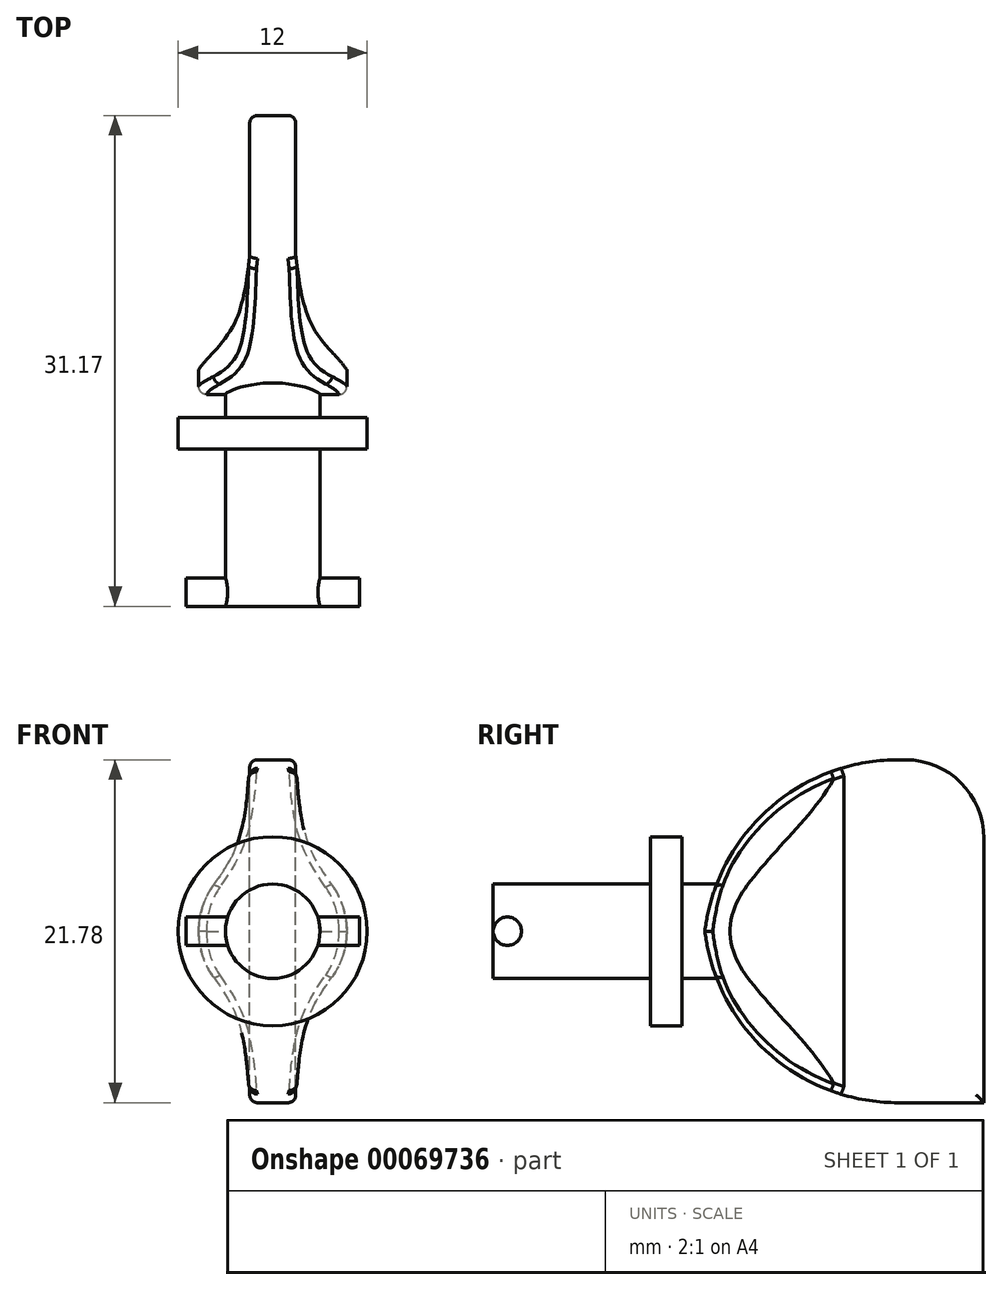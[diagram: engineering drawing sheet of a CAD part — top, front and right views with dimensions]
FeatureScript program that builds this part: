
annotation { "Feature Type Name" : "Feature", "Feature Type Description" : "" }
export const myFeature = defineFeature(function(context is Context, id is Id, definition is map)
    precondition{}
    {
        {
            var Q0;
            Q0=qCreatedBy(makeId("Front.planeOp"),FACE);
            var sketch = newSketch(context, id + "F0", { "sketchPlane" : qUnion([Q0])});
            skCircle(sketch, "E0", {"center": v(0, 0) * mm, "radius": 3 * mm});
            skSolve(sketch);
        }
        {
            var Q0;
            Q0 = qSketchRegion(id + "F0", true);
            extrude(context, id + "F1", {"entities" : qUnion([Q0]), "depth" : 10 * mm});
        }
        {
            var Q0;
            Q0=qCreatedBy(makeId("Right.planeOp"),FACE);
            var sketch = newSketch(context, id + "F2", { "sketchPlane" : qUnion([Q0])});
            skCircle(sketch, "E1", {"center": v(-9.1, 0) * mm, "radius": 0.9 * mm});
            skSolve(sketch);
        }
        {
            var Q0;
            Q0 = qSketchRegion(id + "F2", true);
            extrude(context, id + "F3", {"entities" : qUnion([Q0]), "operationType" : NewBodyOperationType.ADD, "endBound" : BoundingType.SYMMETRIC, "depth" : 11 * mm});
        }
        {
            var Q0;
            Q0=qCreatedBy(makeId("Front.planeOp"),FACE);
            var sketch = newSketch(context, id + "F4", { "sketchPlane" : qUnion([Q0])});
            skCircle(sketch, "E2", {"center": v(0, 0) * mm, "radius": 6 * mm});
            skSolve(sketch);
        }
        {
            var Q0;
            Q0 = qSketchRegion(id + "F4", true);
            extrude(context, id + "F5", {"entities" : qUnion([Q0]), "operationType" : NewBodyOperationType.ADD, "oppositeDirection" : true, "depth" : 2 * mm});
        }
        {
            var Q0;
            Q0=qCreatedBy(makeId("Front.planeOp"),FACE);
            var sketch = newSketch(context, id + "F6", { "sketchPlane" : qUnion([Q0])});
            skCircle(sketch, "E3", {"center": v(0, 0) * mm, "radius": 3 * mm});
            skSolve(sketch);
        }
        {
            var Q0;
            Q0 = qSketchRegion(id + "F6", true);
            extrude(context, id + "F7", {"entities" : qUnion([Q0]), "operationType" : NewBodyOperationType.ADD, "oppositeDirection" : true, "depth" : 4 * mm});
        }
        {
            var Q0;
            Q0=qCreatedBy(makeId("Right.planeOp"),FACE);
            var sketch = newSketch(context, id + "F8", { "sketchPlane" : qUnion([Q0])});
            skLineSegment(sketch, "E4.bottom", {"start": v(3.36, 10.9) * mm, "end": v(21.17, 10.9) * mm});
            skLineSegment(sketch, "E4.top", {"start": v(3.36, -12.24) * mm, "end": v(21.17, -12.24) * mm});
            skLineSegment(sketch, "E4.left", {"start": v(3.36, 10.9) * mm, "end": v(3.36, -12.24) * mm});
            skLineSegment(sketch, "E4.right", {"start": v(21.17, 10.9) * mm, "end": v(21.17, -12.24) * mm});
            skSolve(sketch);
        }
        {
            var Q0;
            Q0 = qSketchRegion(id + "F8", true);
            extrude(context, id + "F9", {"entities" : qUnion([Q0]), "operationType" : NewBodyOperationType.ADD, "endBound" : BoundingType.SYMMETRIC, "depth" : 13 * mm});
        }
        {
            var Q0;
            Q0=makeQuery(id+"F9.opExtrude","SWEPT_FACE",FACE,{"disambiguationData":[OSD([sQuery(id+"F8.wireOp",EDGE,"E4.right")])]});
            var sketch = newSketch(context, id + "F10", { "sketchPlane" : qUnion([Q0])});
            skFitSpline(sketch, "E5", {"points": [v(5.08, 0) * mm, v(4.54, 1.74) * mm, v(2.44, 5.09) * mm, v(1.46, 10.9) * mm], "startDerivative": vector(-1.3, 7.15) * mm, "endDerivative": vector(-0.86, 14.8) * mm});
            skLineSegment(sketch, "E6", {"start": v(1.46, 10.9) * mm, "end": v(6.5, 10.9) * mm});
            skLineSegment(sketch, "E7", {"start": v(6.5, 10.9) * mm, "end": v(6.5, 0) * mm});
            skLineSegment(sketch, "E8", {"start": v(6.5, 0) * mm, "end": v(5.08, 0) * mm});
            skFitSpline(sketch, "E9.MirrorCS", {"points": [v(-5.08, 0) * mm, v(-4.54, 1.74) * mm, v(-2.44, 5.09) * mm, v(-1.46, 10.9) * mm], "startDerivative": vector(1.3, 7.15) * mm, "endDerivative": vector(0.86, 14.8) * mm});
            skLineSegment(sketch, "E10.MirrorCS", {"start": v(-1.46, 10.9) * mm, "end": v(-6.5, 10.9) * mm});
            skLineSegment(sketch, "E11.MirrorCS", {"start": v(-6.5, 10.9) * mm, "end": v(-6.5, 0) * mm});
            skLineSegment(sketch, "E12.MirrorCS", {"start": v(-6.5, 0) * mm, "end": v(-5.08, 0) * mm});
            skFitSpline(sketch, "E13.MirrorCS", {"points": [v(-5.08, 0) * mm, v(-4.54, -1.74) * mm, v(-2.44, -5.09) * mm, v(-1.46, -10.9) * mm], "startDerivative": vector(1.3, -7.15) * mm, "endDerivative": vector(0.86, -14.8) * mm});
            skFitSpline(sketch, "E14.MirrorCS", {"points": [v(5.08, 0) * mm, v(4.54, -1.74) * mm, v(2.44, -5.09) * mm, v(1.46, -10.9) * mm], "startDerivative": vector(-1.3, -7.15) * mm, "endDerivative": vector(-0.86, -14.8) * mm});
            skLineSegment(sketch, "E15.MirrorCS", {"start": v(6.5, -10.9) * mm, "end": v(6.5, 0) * mm});
            skLineSegment(sketch, "E16.MirrorCS", {"start": v(-1.46, -10.9) * mm, "end": v(-6.5, -10.9) * mm});
            skLineSegment(sketch, "E17.MirrorCS", {"start": v(1.46, -10.9) * mm, "end": v(6.5, -10.9) * mm});
            skSolve(sketch);
        }
        {
            var Q0;
            Q0=makeQuery(id+"F10.imprint","IMPRINT",FACE,{"disambiguationData":[TD([[makeQuery(id+"F10.imprint","IMPRINT",EDGE,{"derivedFrom":sQuery(id+"F10.wireOp",EDGE,"E5")}),-1.0]])]});
            var Q1;
            Q1=makeQuery(id+"F10.imprint","IMPRINT",FACE,{"disambiguationData":[TD([[makeQuery(id+"F10.imprint","IMPRINT",EDGE,{"derivedFrom":sQuery(id+"F10.wireOp",EDGE,"E9.MirrorCS")}),1.0]])]});
            var Q2;
            {var subQ0=sQuery(id+"F10.wireOp",EDGE,"E12.MirrorCS");Q2=makeQuery(id+"F10.imprint","IMPRINT",FACE,{"disambiguationData":[TD([[makeQuery(id+"F10.imprint","IMPRINT",EDGE,{"derivedFrom":subQ0}),-1.0]])]});}
            var Q3;
            Q3=makeQuery(id+"F10.imprint","IMPRINT",FACE,{"disambiguationData":[TD([[makeQuery(id+"F10.imprint","IMPRINT",EDGE,{"derivedFrom":sQuery(id+"F10.wireOp",EDGE,"E8")}),1.0]])]});
            extrude(context, id + "F11", {"entities" : qUnion([Q0, Q1, Q2, Q3]), "operationType" : NewBodyOperationType.REMOVE, "oppositeDirection" : true, "depth" : 18.1 * mm});
        }
        {
            var Q0;
            Q0=makeQuery(id+"F9.opExtrude","SWEPT_FACE",FACE,{"disambiguationData":[OSD([sQuery(id+"F8.wireOp",EDGE,"E4.right")])]});
            var sketch = newSketch(context, id + "F12", { "sketchPlane" : qUnion([Q0])});
            skLineSegment(sketch, "E18.bottom", {"start": v(-6.5, -10.9) * mm, "end": v(6.5, -10.9) * mm});
            skLineSegment(sketch, "E18.top", {"start": v(-6.5, -12.24) * mm, "end": v(6.5, -12.24) * mm});
            skLineSegment(sketch, "E18.left", {"start": v(-6.5, -10.9) * mm, "end": v(-6.5, -12.24) * mm});
            skLineSegment(sketch, "E18.right", {"start": v(6.5, -10.9) * mm, "end": v(6.5, -12.24) * mm});
            skSolve(sketch);
        }
        {
            var Q0;
            Q0 = qSketchRegion(id + "F12", true);
            extrude(context, id + "F13", {"entities" : qUnion([Q0]), "operationType" : NewBodyOperationType.REMOVE, "oppositeDirection" : true, "depth" : 25 * mm});
        }
        {
            var Q0;
            Q0=makeQuery(id+"F9.opExtrude","SWEPT_FACE",FACE,{"disambiguationData":[OSD([sQuery(id+"F8.wireOp",EDGE,"E4.bottom")])]});
            var sketch = newSketch(context, id + "F14", { "sketchPlane" : qUnion([Q0])});
            skFitSpline(sketch, "E19", {"points": [v(-5.1, 3.39) * mm, v(-4.84, 4.81) * mm, v(-2.65, 7.57) * mm, v(-1.46, 12.27) * mm], "startDerivative": vector(-0.1, 6.11) * mm, "endDerivative": vector(1.43, 12.16) * mm});
            skLineSegment(sketch, "E20", {"start": v(-1.46, 12.27) * mm, "end": v(-1.46, 21.17) * mm});
            skLineSegment(sketch, "E21", {"start": v(-1.46, 21.17) * mm, "end": v(-5.2, 21.17) * mm});
            skLineSegment(sketch, "E22", {"start": v(-5.2, 21.17) * mm, "end": v(-5.1, 3.39) * mm});
            skLineSegment(sketch, "E23.MirrorCS", {"start": v(5.2, 21.17) * mm, "end": v(5.1, 3.39) * mm});
            skLineSegment(sketch, "E24.MirrorCS", {"start": v(1.46, 12.27) * mm, "end": v(1.46, 21.17) * mm});
            skLineSegment(sketch, "E25.MirrorCS", {"start": v(1.46, 21.17) * mm, "end": v(5.2, 21.17) * mm});
            skFitSpline(sketch, "E26.MirrorCS", {"points": [v(5.1, 3.39) * mm, v(4.84, 4.81) * mm, v(2.65, 7.57) * mm, v(1.46, 12.27) * mm], "startDerivative": vector(0.1, 6.11) * mm, "endDerivative": vector(-1.43, 12.16) * mm});
            skSolve(sketch);
        }
        {
            var Q0;
            Q0 = qSketchRegion(id + "F14", true);
            extrude(context, id + "F15", {"entities" : qUnion([Q0]), "operationType" : NewBodyOperationType.REMOVE, "oppositeDirection" : true, "depth" : 25 * mm});
        }
        {
            var Q0;
            Q0=makeQuery(id+"F9.opExtrude","SWEPT_EDGE",EDGE,{"disambiguationData":[OSD([sQuery(id+"F8.wireOp",EDGE,"E4.bottom"),sQuery(id+"F8.wireOp",EDGE,"E4.right")])]});
            var Q1;
            Q1=makeQuery(id+"F13.boolean.opBoolean","COPY",EDGE,{"derivedFrom":makeQuery(id+"F13.opExtrude","CAP_EDGE",EDGE,{"disambiguationData":[OSD([sQuery(id+"F12.wireOp",EDGE,"E18.bottom")])],"isStart":true})});
            fillet(context, id + "F16", {"entities" : qUnion([Q0, Q1]), "radius" : 5 * mm, "tangentPropagation" : true, "allowEdgeOverflow" : false});
        }
        {
            var Q0;
            Q0=makeQuery(id+"F9.opExtrude","SWEPT_EDGE",EDGE,{"disambiguationData":[OSD([sQuery(id+"F8.wireOp",EDGE,"E4.bottom"),sQuery(id+"F8.wireOp",EDGE,"E4.left")])]});
            var Q1;
            Q1=makeQuery(id+"F13.boolean.opBoolean","INTERSECT",EDGE,{"derivedFrom":[makeQuery(id+"F9.opExtrude","SWEPT_FACE",FACE,{"disambiguationData":[OSD([sQuery(id+"F8.wireOp",EDGE,"E4.left")])]}),makeQuery(id+"F13.opExtrude","SWEPT_FACE",FACE,{"disambiguationData":[OSD([sQuery(id+"F12.wireOp",EDGE,"E18.bottom")])]})]});
            fillet(context, id + "F17", {"entities" : qUnion([Q0, Q1]), "radius" : 12.37 * mm, "tangentPropagation" : true, "allowEdgeOverflow" : false});
        }
        {
            var Q0;
            Q0=makeQuery(id+"F11.boolean.opBoolean","COPY",EDGE,{"derivedFrom":makeQuery(id+"F11.opExtrude","SWEPT_EDGE",EDGE,{"disambiguationData":[OSD([sQuery(id+"F10.wireOp",EDGE,"E9.MirrorCS"),sQuery(id+"F10.wireOp",EDGE,"E12.MirrorCS"),sQuery(id+"F10.wireOp",EDGE,"E13.MirrorCS")])]})});
            fillet(context, id + "F18", {"entities" : qUnion([Q0]), "radius" : 5 * mm, "tangentPropagation" : true, "allowEdgeOverflow" : false});
        }
        {
            var Q0;
            Q0=makeQuery(id+"F11.boolean.opBoolean","COPY",EDGE,{"derivedFrom":makeQuery(id+"F11.opExtrude","SWEPT_EDGE",EDGE,{"disambiguationData":[OSD([sQuery(id+"F10.wireOp",EDGE,"E5"),sQuery(id+"F10.wireOp",EDGE,"E8"),sQuery(id+"F10.wireOp",EDGE,"E14.MirrorCS")])]})});
            fillet(context, id + "F19", {"entities" : qUnion([Q0]), "radius" : 5 * mm, "tangentPropagation" : true, "allowEdgeOverflow" : false});
        }
        {
            var Q0;
            Q0=makeQuery(id+"F19.opFillet","BLEND_EDGE",EDGE,{"blendedFrom":[makeQuery(id+"F11.boolean.opBoolean","COPY",EDGE,{"derivedFrom":makeQuery(id+"F11.opExtrude","SWEPT_EDGE",EDGE,{"disambiguationData":[OSD([sQuery(id+"F10.wireOp",EDGE,"E5"),sQuery(id+"F10.wireOp",EDGE,"E8"),sQuery(id+"F10.wireOp",EDGE,"E14.MirrorCS")])]})}),makeQuery(id+"F17.opFillet","BLEND_FACE",FACE,{"disambiguationData":[OSD([sQuery(id+"F8.wireOp",EDGE,"E4.bottom"),sQuery(id+"F8.wireOp",EDGE,"E4.left")])]})],"blendedInto":[makeQuery(id+"F17.opFillet","BLEND_FACE",FACE,{"disambiguationData":[OSD([sQuery(id+"F8.wireOp",EDGE,"E4.bottom"),sQuery(id+"F8.wireOp",EDGE,"E4.left")])]})]});
            var Q1;
            Q1=makeQuery(id+"F19.opFillet","BLEND_EDGE",EDGE,{"blendedFrom":[makeQuery(id+"F11.boolean.opBoolean","COPY",EDGE,{"derivedFrom":makeQuery(id+"F11.opExtrude","SWEPT_EDGE",EDGE,{"disambiguationData":[OSD([sQuery(id+"F10.wireOp",EDGE,"E5"),sQuery(id+"F10.wireOp",EDGE,"E8"),sQuery(id+"F10.wireOp",EDGE,"E14.MirrorCS")])]})}),makeQuery(id+"F17.opFillet","BLEND_FACE",FACE,{"disambiguationData":[OSD([sQuery(id+"F8.wireOp",EDGE,"E4.left"),sQuery(id+"F12.wireOp",EDGE,"E18.bottom")])]})],"blendedInto":[makeQuery(id+"F17.opFillet","BLEND_FACE",FACE,{"disambiguationData":[OSD([sQuery(id+"F8.wireOp",EDGE,"E4.left"),sQuery(id+"F12.wireOp",EDGE,"E18.bottom")])]})]});
            var Q2;
            Q2=makeQuery(id+"F17.opFillet","BLEND_EDGE",EDGE,{"blendedFrom":[makeQuery(id+"F13.boolean.opBoolean","INTERSECT",EDGE,{"derivedFrom":[makeQuery(id+"F9.opExtrude","SWEPT_FACE",FACE,{"disambiguationData":[OSD([sQuery(id+"F8.wireOp",EDGE,"E4.left")])]}),makeQuery(id+"F13.opExtrude","SWEPT_FACE",FACE,{"disambiguationData":[OSD([sQuery(id+"F12.wireOp",EDGE,"E18.bottom")])]})]}),makeQuery(id+"F11.boolean.opBoolean","COPY",FACE,{"derivedFrom":makeQuery(id+"F11.opExtrude","SWEPT_FACE",FACE,{"disambiguationData":[OSD([sQuery(id+"F10.wireOp",EDGE,"E14.MirrorCS")])]})})],"blendedInto":[makeQuery(id+"F11.boolean.opBoolean","COPY",FACE,{"derivedFrom":makeQuery(id+"F11.opExtrude","SWEPT_FACE",FACE,{"disambiguationData":[OSD([sQuery(id+"F10.wireOp",EDGE,"E14.MirrorCS")])]})})]});
            var Q3;
            Q3=makeQuery(id+"F17.opFillet","BLEND_EDGE",EDGE,{"blendedFrom":[makeQuery(id+"F13.boolean.opBoolean","INTERSECT",EDGE,{"derivedFrom":[makeQuery(id+"F9.opExtrude","SWEPT_FACE",FACE,{"disambiguationData":[OSD([sQuery(id+"F8.wireOp",EDGE,"E4.left")])]}),makeQuery(id+"F13.opExtrude","SWEPT_FACE",FACE,{"disambiguationData":[OSD([sQuery(id+"F12.wireOp",EDGE,"E18.bottom")])]})]}),makeQuery(id+"F15.boolean.opBoolean","COPY",FACE,{"derivedFrom":makeQuery(id+"F15.opExtrude","SWEPT_FACE",FACE,{"disambiguationData":[OSD([sQuery(id+"F14.wireOp",EDGE,"E20")])]})})],"blendedInto":[makeQuery(id+"F15.boolean.opBoolean","COPY",FACE,{"derivedFrom":makeQuery(id+"F15.opExtrude","SWEPT_FACE",FACE,{"disambiguationData":[OSD([sQuery(id+"F14.wireOp",EDGE,"E20")])]})})]});
            var Q4;
            Q4=makeQuery(id+"F16.opFillet","BLEND_EDGE",EDGE,{"blendedFrom":[makeQuery(id+"F13.boolean.opBoolean","COPY",EDGE,{"derivedFrom":makeQuery(id+"F13.opExtrude","CAP_EDGE",EDGE,{"disambiguationData":[OSD([sQuery(id+"F12.wireOp",EDGE,"E18.bottom")])],"isStart":true})}),makeQuery(id+"F15.boolean.opBoolean","COPY",FACE,{"derivedFrom":makeQuery(id+"F15.opExtrude","SWEPT_FACE",FACE,{"disambiguationData":[OSD([sQuery(id+"F14.wireOp",EDGE,"E20")])]})})],"blendedInto":[makeQuery(id+"F15.boolean.opBoolean","COPY",FACE,{"derivedFrom":makeQuery(id+"F15.opExtrude","SWEPT_FACE",FACE,{"disambiguationData":[OSD([sQuery(id+"F14.wireOp",EDGE,"E20")])]})})]});
            var Q5;
            Q5=makeQuery(id+"F15.boolean.opBoolean","COPY",EDGE,{"derivedFrom":makeQuery(id+"F15.opExtrude","SWEPT_EDGE",EDGE,{"disambiguationData":[OSD([sQuery(id+"F8.wireOp",EDGE,"E4.bottom"),sQuery(id+"F8.wireOp",EDGE,"E4.right"),sQuery(id+"F14.wireOp",EDGE,"E20"),sQuery(id+"F14.wireOp",EDGE,"E21")])]})});
            var Q6;
            Q6=makeQuery(id+"F16.opFillet","BLEND_EDGE",EDGE,{"blendedFrom":[makeQuery(id+"F9.opExtrude","SWEPT_EDGE",EDGE,{"disambiguationData":[OSD([sQuery(id+"F8.wireOp",EDGE,"E4.bottom"),sQuery(id+"F8.wireOp",EDGE,"E4.right")])]}),makeQuery(id+"F15.boolean.opBoolean","COPY",FACE,{"derivedFrom":makeQuery(id+"F15.opExtrude","SWEPT_FACE",FACE,{"disambiguationData":[OSD([sQuery(id+"F14.wireOp",EDGE,"E20")])]})})],"blendedInto":[makeQuery(id+"F15.boolean.opBoolean","COPY",FACE,{"derivedFrom":makeQuery(id+"F15.opExtrude","SWEPT_FACE",FACE,{"disambiguationData":[OSD([sQuery(id+"F14.wireOp",EDGE,"E20")])]})})]});
            var Q7;
            Q7=makeQuery(id+"F17.opFillet","BLEND_EDGE",EDGE,{"blendedFrom":[makeQuery(id+"F9.opExtrude","SWEPT_EDGE",EDGE,{"disambiguationData":[OSD([sQuery(id+"F8.wireOp",EDGE,"E4.bottom"),sQuery(id+"F8.wireOp",EDGE,"E4.left")])]}),makeQuery(id+"F11.boolean.opBoolean","COPY",FACE,{"derivedFrom":makeQuery(id+"F11.opExtrude","SWEPT_FACE",FACE,{"disambiguationData":[OSD([sQuery(id+"F10.wireOp",EDGE,"E5")])]})})],"blendedInto":[makeQuery(id+"F11.boolean.opBoolean","COPY",FACE,{"derivedFrom":makeQuery(id+"F11.opExtrude","SWEPT_FACE",FACE,{"disambiguationData":[OSD([sQuery(id+"F10.wireOp",EDGE,"E5")])]})})]});
            var Q8;
            {var subQ0=sQuery(id+"F14.wireOp",EDGE,"E19");Q8=makeQuery(id+"F17.opFillet","BLEND_EDGE",EDGE,{"blendedFrom":[makeQuery(id+"F13.boolean.opBoolean","INTERSECT",EDGE,{"derivedFrom":[makeQuery(id+"F9.opExtrude","SWEPT_FACE",FACE,{"disambiguationData":[OSD([sQuery(id+"F8.wireOp",EDGE,"E4.left")])]}),makeQuery(id+"F13.opExtrude","SWEPT_FACE",FACE,{"disambiguationData":[OSD([sQuery(id+"F12.wireOp",EDGE,"E18.bottom")])]})]}),makeQuery(id+"F15.boolean.opBoolean","COPY",FACE,{"derivedFrom":makeQuery(id+"F15.opExtrude","SWEPT_FACE",FACE,{"disambiguationData":[OSD([subQ0]),TDD([makeQuery(id+"F14.imprint","IMPRINT",EDGE,{"disambiguationData":[TD([[makeQuery(id+"F14.imprint","INTERSECT",VERTEX,{"disambiguationData":[OD(1.0)],"derivedFrom":[subQ0,sQuery(id+"F14.wireOp",EDGE,"E22")]}),-1.0]])],"derivedFrom":subQ0})])]})})],"blendedInto":[makeQuery(id+"F15.boolean.opBoolean","COPY",FACE,{"derivedFrom":makeQuery(id+"F15.opExtrude","SWEPT_FACE",FACE,{"disambiguationData":[OSD([subQ0]),TDD([makeQuery(id+"F14.imprint","IMPRINT",EDGE,{"disambiguationData":[TD([[makeQuery(id+"F14.imprint","INTERSECT",VERTEX,{"disambiguationData":[OD(1.0)],"derivedFrom":[subQ0,sQuery(id+"F14.wireOp",EDGE,"E22")]}),-1.0]])],"derivedFrom":subQ0})])]})})]});}
            var Q9;
            {var subQ2=sQuery(id+"F8.wireOp",EDGE,"E4.right");var subQ3=sQuery(id+"F10.wireOp",EDGE,"E14.MirrorCS");Q9=makeQuery(id+"F15.boolean.opBoolean","SPLIT",EDGE,{"disambiguationData":[TD([makeQuery(id+"F9.opExtrude","SWEPT_FACE",FACE,{"disambiguationData":[OSD([subQ2])]})])],"derivedFrom":makeQuery(id+"F11.boolean.opBoolean","COPY",EDGE,{"derivedFrom":makeQuery(id+"F11.opExtrude","SWEPT_EDGE",EDGE,{"disambiguationData":[OSD([subQ3,sQuery(id+"F10.wireOp",EDGE,"E17.MirrorCS")])]})})});}
            var Q10;
            Q10=makeQuery(id+"F17.opFillet","BLEND_EDGE",EDGE,{"blendedFrom":[makeQuery(id+"F9.opExtrude","SWEPT_EDGE",EDGE,{"disambiguationData":[OSD([sQuery(id+"F8.wireOp",EDGE,"E4.bottom"),sQuery(id+"F8.wireOp",EDGE,"E4.left")])]}),makeQuery(id+"F15.boolean.opBoolean","COPY",FACE,{"derivedFrom":makeQuery(id+"F15.opExtrude","SWEPT_FACE",FACE,{"disambiguationData":[OSD([sQuery(id+"F14.wireOp",EDGE,"E20")])]})})],"blendedInto":[makeQuery(id+"F15.boolean.opBoolean","COPY",FACE,{"derivedFrom":makeQuery(id+"F15.opExtrude","SWEPT_FACE",FACE,{"disambiguationData":[OSD([sQuery(id+"F14.wireOp",EDGE,"E20")])]})})]});
            var Q11;
            {var subQ0=sQuery(id+"F14.wireOp",EDGE,"E19");var subQ1=sQuery(id+"F8.wireOp",EDGE,"E4.bottom");Q11=makeQuery(id+"F17.opFillet","BLEND_EDGE",EDGE,{"blendedFrom":[makeQuery(id+"F9.opExtrude","SWEPT_EDGE",EDGE,{"disambiguationData":[OSD([subQ1,sQuery(id+"F8.wireOp",EDGE,"E4.left")])]}),makeQuery(id+"F15.boolean.opBoolean","COPY",FACE,{"derivedFrom":makeQuery(id+"F15.opExtrude","SWEPT_FACE",FACE,{"disambiguationData":[OSD([subQ0]),TDD([makeQuery(id+"F14.imprint","IMPRINT",EDGE,{"disambiguationData":[TD([[makeQuery(id+"F14.imprint","INTERSECT",VERTEX,{"disambiguationData":[OD(1.0)],"derivedFrom":[subQ0,sQuery(id+"F14.wireOp",EDGE,"E22")]}),-1.0]])],"derivedFrom":subQ0})])]})})],"blendedInto":[makeQuery(id+"F15.boolean.opBoolean","COPY",FACE,{"derivedFrom":makeQuery(id+"F15.opExtrude","SWEPT_FACE",FACE,{"disambiguationData":[OSD([subQ0]),TDD([makeQuery(id+"F14.imprint","IMPRINT",EDGE,{"disambiguationData":[TD([[makeQuery(id+"F14.imprint","INTERSECT",VERTEX,{"disambiguationData":[OD(1.0)],"derivedFrom":[subQ0,sQuery(id+"F14.wireOp",EDGE,"E22")]}),-1.0]])],"derivedFrom":subQ0})])]})})]});}
            var Q12;
            Q12=makeQuery(id+"F15.boolean.opBoolean","MERGE",EDGE,{"derivedFrom":[makeQuery(id+"F11.boolean.opBoolean","COPY",EDGE,{"derivedFrom":makeQuery(id+"F11.opExtrude","SWEPT_EDGE",EDGE,{"disambiguationData":[OSD([sQuery(id+"F8.wireOp",EDGE,"E4.bottom"),sQuery(id+"F8.wireOp",EDGE,"E4.right"),sQuery(id+"F10.wireOp",EDGE,"E5"),sQuery(id+"F10.wireOp",EDGE,"E6")])]})}),makeQuery(id+"F15.opExtrude","CAP_EDGE",EDGE,{"disambiguationData":[OSD([sQuery(id+"F14.wireOp",EDGE,"E20")])],"isStart":true})]});
            fillet(context, id + "F20", {"entities" : qUnion([Q0, Q1, Q2, Q3, Q4, Q5, Q6, Q7, Q8, Q9, Q10, Q11, Q12]), "radius" : 0.5 * mm, "tangentPropagation" : true, "allowEdgeOverflow" : false});
        }
        {
            var Q0;
            Q0=makeQuery(id+"F15.boolean.opBoolean","COPY",EDGE,{"derivedFrom":makeQuery(id+"F15.opExtrude","SWEPT_EDGE",EDGE,{"disambiguationData":[OSD([sQuery(id+"F8.wireOp",EDGE,"E4.bottom"),sQuery(id+"F8.wireOp",EDGE,"E4.right"),sQuery(id+"F14.wireOp",EDGE,"E24.MirrorCS"),sQuery(id+"F14.wireOp",EDGE,"E25.MirrorCS")])]})});
            var Q1;
            Q1=makeQuery(id+"F16.opFillet","BLEND_EDGE",EDGE,{"blendedFrom":[makeQuery(id+"F9.opExtrude","SWEPT_EDGE",EDGE,{"disambiguationData":[OSD([sQuery(id+"F8.wireOp",EDGE,"E4.bottom"),sQuery(id+"F8.wireOp",EDGE,"E4.right")])]}),makeQuery(id+"F15.boolean.opBoolean","COPY",FACE,{"derivedFrom":makeQuery(id+"F15.opExtrude","SWEPT_FACE",FACE,{"disambiguationData":[OSD([sQuery(id+"F14.wireOp",EDGE,"E24.MirrorCS")])]})})],"blendedInto":[makeQuery(id+"F15.boolean.opBoolean","COPY",FACE,{"derivedFrom":makeQuery(id+"F15.opExtrude","SWEPT_FACE",FACE,{"disambiguationData":[OSD([sQuery(id+"F14.wireOp",EDGE,"E24.MirrorCS")])]})})]});
            var Q2;
            Q2=makeQuery(id+"F17.opFillet","BLEND_EDGE",EDGE,{"blendedFrom":[makeQuery(id+"F9.opExtrude","SWEPT_EDGE",EDGE,{"disambiguationData":[OSD([sQuery(id+"F8.wireOp",EDGE,"E4.bottom"),sQuery(id+"F8.wireOp",EDGE,"E4.left")])]}),makeQuery(id+"F15.boolean.opBoolean","COPY",FACE,{"derivedFrom":makeQuery(id+"F15.opExtrude","SWEPT_FACE",FACE,{"disambiguationData":[OSD([sQuery(id+"F14.wireOp",EDGE,"E24.MirrorCS")])]})})],"blendedInto":[makeQuery(id+"F15.boolean.opBoolean","COPY",FACE,{"derivedFrom":makeQuery(id+"F15.opExtrude","SWEPT_FACE",FACE,{"disambiguationData":[OSD([sQuery(id+"F14.wireOp",EDGE,"E24.MirrorCS")])]})})]});
            var Q3;
            Q3=makeQuery(id+"F17.opFillet","BLEND_EDGE",EDGE,{"blendedFrom":[makeQuery(id+"F9.opExtrude","SWEPT_EDGE",EDGE,{"disambiguationData":[OSD([sQuery(id+"F8.wireOp",EDGE,"E4.bottom"),sQuery(id+"F8.wireOp",EDGE,"E4.left")])]}),makeQuery(id+"F11.boolean.opBoolean","COPY",FACE,{"derivedFrom":makeQuery(id+"F11.opExtrude","SWEPT_FACE",FACE,{"disambiguationData":[OSD([sQuery(id+"F10.wireOp",EDGE,"E9.MirrorCS")])]})})],"blendedInto":[makeQuery(id+"F11.boolean.opBoolean","COPY",FACE,{"derivedFrom":makeQuery(id+"F11.opExtrude","SWEPT_FACE",FACE,{"disambiguationData":[OSD([sQuery(id+"F10.wireOp",EDGE,"E9.MirrorCS")])]})})]});
            var Q4;
            Q4=makeQuery(id+"F18.opFillet","BLEND_EDGE",EDGE,{"blendedFrom":[makeQuery(id+"F11.boolean.opBoolean","COPY",EDGE,{"derivedFrom":makeQuery(id+"F11.opExtrude","SWEPT_EDGE",EDGE,{"disambiguationData":[OSD([sQuery(id+"F10.wireOp",EDGE,"E9.MirrorCS"),sQuery(id+"F10.wireOp",EDGE,"E12.MirrorCS"),sQuery(id+"F10.wireOp",EDGE,"E13.MirrorCS")])]})}),makeQuery(id+"F17.opFillet","BLEND_FACE",FACE,{"disambiguationData":[OSD([sQuery(id+"F8.wireOp",EDGE,"E4.bottom"),sQuery(id+"F8.wireOp",EDGE,"E4.left")])]})],"blendedInto":[makeQuery(id+"F17.opFillet","BLEND_FACE",FACE,{"disambiguationData":[OSD([sQuery(id+"F8.wireOp",EDGE,"E4.bottom"),sQuery(id+"F8.wireOp",EDGE,"E4.left")])]})]});
            var Q5;
            Q5=makeQuery(id+"F18.opFillet","BLEND_EDGE",EDGE,{"blendedFrom":[makeQuery(id+"F11.boolean.opBoolean","COPY",EDGE,{"derivedFrom":makeQuery(id+"F11.opExtrude","SWEPT_EDGE",EDGE,{"disambiguationData":[OSD([sQuery(id+"F10.wireOp",EDGE,"E9.MirrorCS"),sQuery(id+"F10.wireOp",EDGE,"E12.MirrorCS"),sQuery(id+"F10.wireOp",EDGE,"E13.MirrorCS")])]})}),makeQuery(id+"F17.opFillet","BLEND_FACE",FACE,{"disambiguationData":[OSD([sQuery(id+"F8.wireOp",EDGE,"E4.left"),sQuery(id+"F12.wireOp",EDGE,"E18.bottom")])]})],"blendedInto":[makeQuery(id+"F17.opFillet","BLEND_FACE",FACE,{"disambiguationData":[OSD([sQuery(id+"F8.wireOp",EDGE,"E4.left"),sQuery(id+"F12.wireOp",EDGE,"E18.bottom")])]})]});
            var Q6;
            Q6=makeQuery(id+"F17.opFillet","BLEND_EDGE",EDGE,{"blendedFrom":[makeQuery(id+"F13.boolean.opBoolean","INTERSECT",EDGE,{"derivedFrom":[makeQuery(id+"F9.opExtrude","SWEPT_FACE",FACE,{"disambiguationData":[OSD([sQuery(id+"F8.wireOp",EDGE,"E4.left")])]}),makeQuery(id+"F13.opExtrude","SWEPT_FACE",FACE,{"disambiguationData":[OSD([sQuery(id+"F12.wireOp",EDGE,"E18.bottom")])]})]}),makeQuery(id+"F11.boolean.opBoolean","COPY",FACE,{"derivedFrom":makeQuery(id+"F11.opExtrude","SWEPT_FACE",FACE,{"disambiguationData":[OSD([sQuery(id+"F10.wireOp",EDGE,"E13.MirrorCS")])]})})],"blendedInto":[makeQuery(id+"F11.boolean.opBoolean","COPY",FACE,{"derivedFrom":makeQuery(id+"F11.opExtrude","SWEPT_FACE",FACE,{"disambiguationData":[OSD([sQuery(id+"F10.wireOp",EDGE,"E13.MirrorCS")])]})})]});
            var Q7;
            Q7=makeQuery(id+"F17.opFillet","BLEND_EDGE",EDGE,{"blendedFrom":[makeQuery(id+"F13.boolean.opBoolean","INTERSECT",EDGE,{"derivedFrom":[makeQuery(id+"F9.opExtrude","SWEPT_FACE",FACE,{"disambiguationData":[OSD([sQuery(id+"F8.wireOp",EDGE,"E4.left")])]}),makeQuery(id+"F13.opExtrude","SWEPT_FACE",FACE,{"disambiguationData":[OSD([sQuery(id+"F12.wireOp",EDGE,"E18.bottom")])]})]}),makeQuery(id+"F15.boolean.opBoolean","COPY",FACE,{"derivedFrom":makeQuery(id+"F15.opExtrude","SWEPT_FACE",FACE,{"disambiguationData":[OSD([sQuery(id+"F14.wireOp",EDGE,"E24.MirrorCS")])]})})],"blendedInto":[makeQuery(id+"F15.boolean.opBoolean","COPY",FACE,{"derivedFrom":makeQuery(id+"F15.opExtrude","SWEPT_FACE",FACE,{"disambiguationData":[OSD([sQuery(id+"F14.wireOp",EDGE,"E24.MirrorCS")])]})})]});
            var Q8;
            Q8=makeQuery(id+"F16.opFillet","BLEND_EDGE",EDGE,{"blendedFrom":[makeQuery(id+"F13.boolean.opBoolean","COPY",EDGE,{"derivedFrom":makeQuery(id+"F13.opExtrude","CAP_EDGE",EDGE,{"disambiguationData":[OSD([sQuery(id+"F12.wireOp",EDGE,"E18.bottom")])],"isStart":true})}),makeQuery(id+"F15.boolean.opBoolean","COPY",FACE,{"derivedFrom":makeQuery(id+"F15.opExtrude","SWEPT_FACE",FACE,{"disambiguationData":[OSD([sQuery(id+"F14.wireOp",EDGE,"E24.MirrorCS")])]})})],"blendedInto":[makeQuery(id+"F15.boolean.opBoolean","COPY",FACE,{"derivedFrom":makeQuery(id+"F15.opExtrude","SWEPT_FACE",FACE,{"disambiguationData":[OSD([sQuery(id+"F14.wireOp",EDGE,"E24.MirrorCS")])]})})]});
            var Q9;
            {var subQ0=sQuery(id+"F14.wireOp",EDGE,"E26.MirrorCS");var subQ1=sQuery(id+"F8.wireOp",EDGE,"E4.bottom");Q9=makeQuery(id+"F17.opFillet","BLEND_EDGE",EDGE,{"blendedFrom":[makeQuery(id+"F9.opExtrude","SWEPT_EDGE",EDGE,{"disambiguationData":[OSD([subQ1,sQuery(id+"F8.wireOp",EDGE,"E4.left")])]}),makeQuery(id+"F15.boolean.opBoolean","COPY",FACE,{"derivedFrom":makeQuery(id+"F15.opExtrude","SWEPT_FACE",FACE,{"disambiguationData":[OSD([subQ0]),TDD([makeQuery(id+"F14.imprint","IMPRINT",EDGE,{"disambiguationData":[TD([[makeQuery(id+"F14.imprint","INTERSECT",VERTEX,{"disambiguationData":[OD(1.0)],"derivedFrom":[sQuery(id+"F14.wireOp",EDGE,"E23.MirrorCS"),subQ0]}),-1.0]])],"derivedFrom":subQ0})])]})})],"blendedInto":[makeQuery(id+"F15.boolean.opBoolean","COPY",FACE,{"derivedFrom":makeQuery(id+"F15.opExtrude","SWEPT_FACE",FACE,{"disambiguationData":[OSD([subQ0]),TDD([makeQuery(id+"F14.imprint","IMPRINT",EDGE,{"disambiguationData":[TD([[makeQuery(id+"F14.imprint","INTERSECT",VERTEX,{"disambiguationData":[OD(1.0)],"derivedFrom":[sQuery(id+"F14.wireOp",EDGE,"E23.MirrorCS"),subQ0]}),-1.0]])],"derivedFrom":subQ0})])]})})]});}
            var Q10;
            Q10=makeQuery(id+"F15.boolean.opBoolean","MERGE",EDGE,{"derivedFrom":[makeQuery(id+"F11.boolean.opBoolean","COPY",EDGE,{"derivedFrom":makeQuery(id+"F11.opExtrude","SWEPT_EDGE",EDGE,{"disambiguationData":[OSD([sQuery(id+"F8.wireOp",EDGE,"E4.bottom"),sQuery(id+"F8.wireOp",EDGE,"E4.right"),sQuery(id+"F10.wireOp",EDGE,"E9.MirrorCS"),sQuery(id+"F10.wireOp",EDGE,"E10.MirrorCS")])]})}),makeQuery(id+"F15.opExtrude","CAP_EDGE",EDGE,{"disambiguationData":[OSD([sQuery(id+"F14.wireOp",EDGE,"E24.MirrorCS")])],"isStart":true})]});
            var Q11;
            {var subQ0=sQuery(id+"F14.wireOp",EDGE,"E26.MirrorCS");Q11=makeQuery(id+"F17.opFillet","BLEND_EDGE",EDGE,{"blendedFrom":[makeQuery(id+"F13.boolean.opBoolean","INTERSECT",EDGE,{"derivedFrom":[makeQuery(id+"F9.opExtrude","SWEPT_FACE",FACE,{"disambiguationData":[OSD([sQuery(id+"F8.wireOp",EDGE,"E4.left")])]}),makeQuery(id+"F13.opExtrude","SWEPT_FACE",FACE,{"disambiguationData":[OSD([sQuery(id+"F12.wireOp",EDGE,"E18.bottom")])]})]}),makeQuery(id+"F15.boolean.opBoolean","COPY",FACE,{"derivedFrom":makeQuery(id+"F15.opExtrude","SWEPT_FACE",FACE,{"disambiguationData":[OSD([subQ0]),TDD([makeQuery(id+"F14.imprint","IMPRINT",EDGE,{"disambiguationData":[TD([[makeQuery(id+"F14.imprint","INTERSECT",VERTEX,{"disambiguationData":[OD(1.0)],"derivedFrom":[sQuery(id+"F14.wireOp",EDGE,"E23.MirrorCS"),subQ0]}),-1.0]])],"derivedFrom":subQ0})])]})})],"blendedInto":[makeQuery(id+"F15.boolean.opBoolean","COPY",FACE,{"derivedFrom":makeQuery(id+"F15.opExtrude","SWEPT_FACE",FACE,{"disambiguationData":[OSD([subQ0]),TDD([makeQuery(id+"F14.imprint","IMPRINT",EDGE,{"disambiguationData":[TD([[makeQuery(id+"F14.imprint","INTERSECT",VERTEX,{"disambiguationData":[OD(1.0)],"derivedFrom":[sQuery(id+"F14.wireOp",EDGE,"E23.MirrorCS"),subQ0]}),-1.0]])],"derivedFrom":subQ0})])]})})]});}
            var Q12;
            {var subQ1=sQuery(id+"F10.wireOp",EDGE,"E13.MirrorCS");var subQ2=sQuery(id+"F8.wireOp",EDGE,"E4.right");Q12=makeQuery(id+"F15.boolean.opBoolean","SPLIT",EDGE,{"disambiguationData":[TD([makeQuery(id+"F9.opExtrude","SWEPT_FACE",FACE,{"disambiguationData":[OSD([subQ2])]})])],"derivedFrom":makeQuery(id+"F11.boolean.opBoolean","COPY",EDGE,{"derivedFrom":makeQuery(id+"F11.opExtrude","SWEPT_EDGE",EDGE,{"disambiguationData":[OSD([subQ1,sQuery(id+"F10.wireOp",EDGE,"E16.MirrorCS")])]})})});}
            fillet(context, id + "F21", {"entities" : qUnion([Q0, Q1, Q2, Q3, Q4, Q5, Q6, Q7, Q8, Q9, Q10, Q11, Q12]), "radius" : 0.5 * mm, "tangentPropagation" : true, "allowEdgeOverflow" : false});
        }
    });
